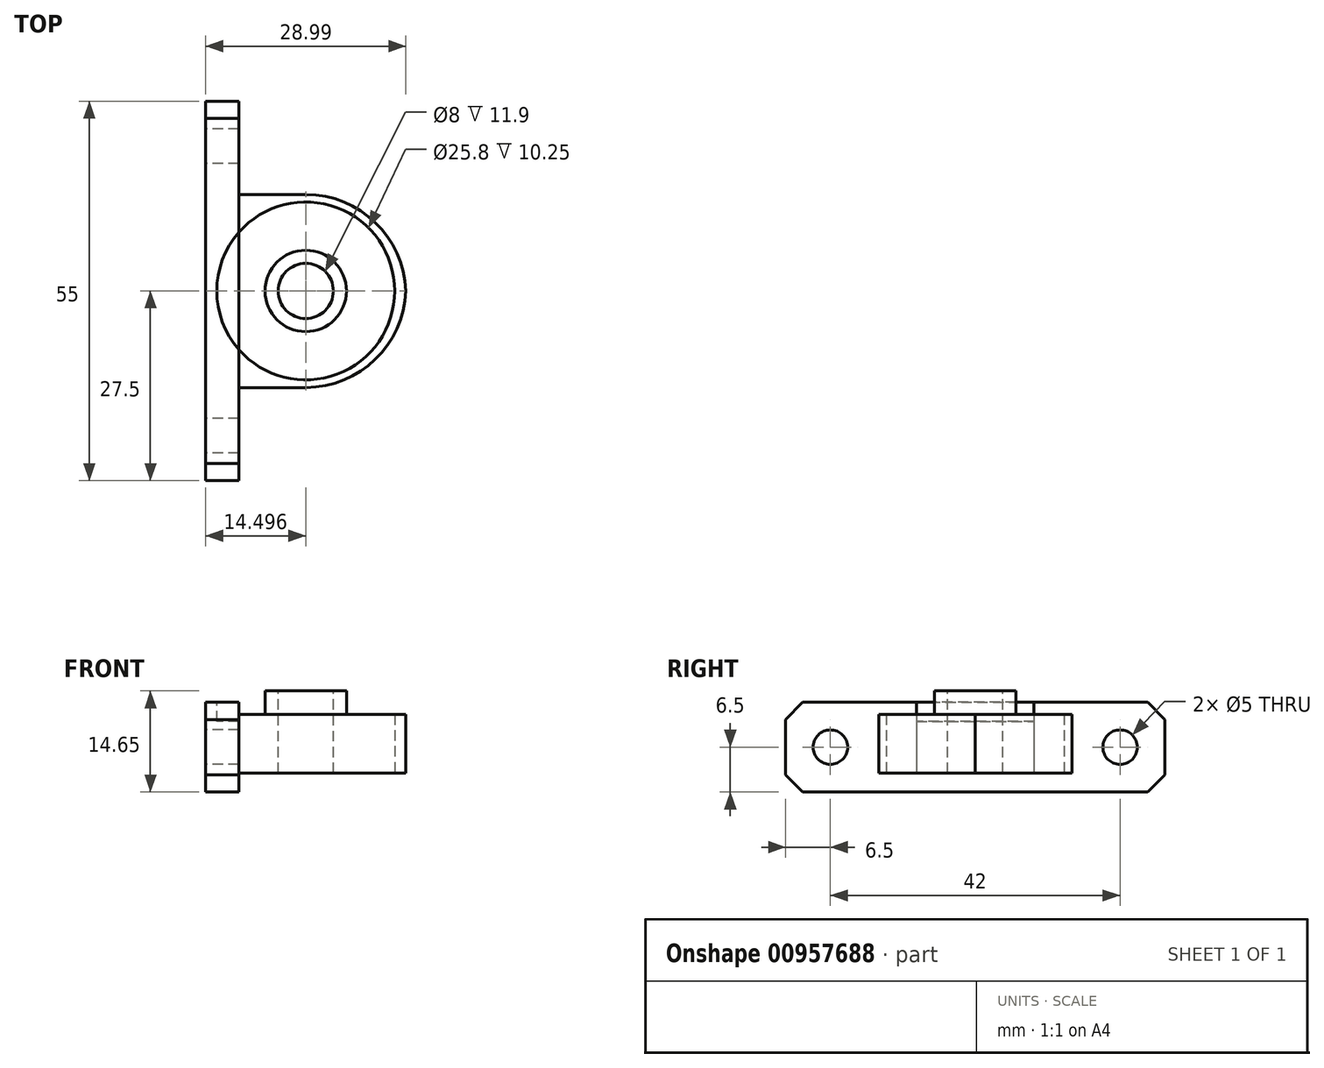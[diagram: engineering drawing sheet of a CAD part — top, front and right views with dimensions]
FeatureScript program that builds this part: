
annotation { "Feature Type Name" : "Feature", "Feature Type Description" : "" }
export const myFeature = defineFeature(function(context is Context, id is Id, definition is map)
    precondition{}
    {
        {
            var Q0;
            Q0=qCreatedBy(makeId("Right.planeOp"),FACE);
            var sketch = newSketch(context, id + "F0", { "sketchPlane" : qUnion([Q0])});
            skLineSegment(sketch, "E0.bottom", {"start": v(0, 0) * mm, "end": v(55, 0) * mm});
            skLineSegment(sketch, "E0.top", {"start": v(0, -13) * mm, "end": v(55, -13) * mm});
            skLineSegment(sketch, "E0.left", {"start": v(0, 0) * mm, "end": v(0, -13) * mm});
            skLineSegment(sketch, "E0.right", {"start": v(55, 0) * mm, "end": v(55, -13) * mm});
            skLineSegment(sketch, "E1", {"start": v(27.5, 0) * mm, "end": v(27.5, -13) * mm, "construction": true});
            skCircle(sketch, "E2", {"center": v(48.5, -6.5) * mm, "radius": 2.5 * mm});
            skLineSegment(sketch, "E3", {"start": v(0, -6.5) * mm, "end": v(55, -6.5) * mm, "construction": true});
            skCircle(sketch, "E4.MirrorC", {"center": v(6.5, -6.5) * mm, "radius": 2.5 * mm});
            skSolve(sketch);
        }
        {
            var Q0;
            Q0 = qSketchRegion(id + "F0", true);
            extrude(context, id + "F1", {"entities" : qUnion([Q0]), "depth" : 4.8 * mm, "offsetDistance" : 25 * mm});
        }
        {
            var Q0;
            Q0 = qSketchRegion(id + "F0", true);
            extrude(context, id + "F2", {"entities" : qUnion([Q0]), "operationType" : NewBodyOperationType.REMOVE, "oppositeDirection" : true, "depth" : 25 * mm, "offsetDistance" : 25 * mm});
        }
        {
            var Q0;
            Q0=makeQuery(id+"F1.opExtrude","SWEPT_EDGE",EDGE,{"disambiguationData":[OSD([sQuery(id+"F0.wireOp",EDGE,"E0.bottom"),sQuery(id+"F0.wireOp",EDGE,"E0.left")])]});
            var Q1;
            Q1=makeQuery(id+"F1.opExtrude","SWEPT_EDGE",EDGE,{"disambiguationData":[OSD([sQuery(id+"F0.wireOp",EDGE,"E0.top"),sQuery(id+"F0.wireOp",EDGE,"E0.left")])]});
            var Q2;
            Q2=makeQuery(id+"F1.opExtrude","SWEPT_EDGE",EDGE,{"disambiguationData":[OSD([sQuery(id+"F0.wireOp",EDGE,"E0.bottom"),sQuery(id+"F0.wireOp",EDGE,"E0.right")])]});
            var Q3;
            Q3=makeQuery(id+"F1.opExtrude","SWEPT_EDGE",EDGE,{"disambiguationData":[OSD([sQuery(id+"F0.wireOp",EDGE,"E0.top"),sQuery(id+"F0.wireOp",EDGE,"E0.right")])]});
            chamfer(context, id + "F3", {"entities" : qUnion([Q0, Q1, Q2, Q3]), "width" : 2.5 * mm, "tangentPropagation" : true});
        }
        {
            var Q0;
            Q0=makeQuery(id+"F1.opExtrude","CAP_FACE",FACE,{"disambiguationData":[OSD([sQuery(id+"F0.wireOp",EDGE,"E0.bottom"),sQuery(id+"F0.wireOp",EDGE,"E0.top"),sQuery(id+"F0.wireOp",EDGE,"E0.left"),sQuery(id+"F0.wireOp",EDGE,"E0.right"),sQuery(id+"F0.wireOp",EDGE,"E2"),sQuery(id+"F0.wireOp",EDGE,"E4.MirrorC")])],"isStart":false});
            var sketch = newSketch(context, id + "F4", { "sketchPlane" : qUnion([Q0])});
            skLineSegment(sketch, "E5.bottom", {"start": v(41.5, -11.25) * mm, "end": v(13.5, -11.25) * mm});
            skLineSegment(sketch, "E5.top", {"start": v(41.5, -1.75) * mm, "end": v(13.5, -1.75) * mm});
            skLineSegment(sketch, "E5.left", {"start": v(41.5, -11.25) * mm, "end": v(41.5, -1.75) * mm});
            skLineSegment(sketch, "E5.right", {"start": v(13.5, -11.25) * mm, "end": v(13.5, -1.75) * mm});
            skPoint(sketch, "E5.middle", {"position": v(27.5, -6.5) * mm});
            skPoint(sketch, "E5.middle.positionSnap0", {"position": v(0, -6.5) * mm});
            skPoint(sketch, "E5.middle.positionSnap1", {"position": v(27.5, -13) * mm});
            skPoint(sketch, "E5.centerSnap0", {"position": v(0, -6.5) * mm});
            skPoint(sketch, "E5.centerSnap1", {"position": v(27.5, -13) * mm});
            skSolve(sketch);
        }
        {
            var Q0;
            Q0 = qSketchRegion(id + "F4", true);
            extrude(context, id + "F5", {"entities" : qUnion([Q0]), "operationType" : NewBodyOperationType.ADD, "depth" : 24.2 * mm, "offsetDistance" : 25 * mm});
        }
        {
            var Q0;
            Q0=makeQuery(id+"F5.opExtrude","CAP_EDGE",EDGE,{"disambiguationData":[OSD([sQuery(id+"F4.wireOp",EDGE,"E5.right")])],"isStart":false});
            var Q1;
            Q1=makeQuery(id+"F5.opExtrude","CAP_EDGE",EDGE,{"disambiguationData":[OSD([sQuery(id+"F4.wireOp",EDGE,"E5.left")])],"isStart":false});
            fillet(context, id + "F6", {"entities" : qUnion([Q0, Q1]), "radius" : 14.5 * mm, "tangentPropagation" : true, "allowEdgeOverflow" : false});
        }
        {
            var Q0;
            Q0=makeQuery(id+"F5.opExtrude","SWEPT_FACE",FACE,{"disambiguationData":[OSD([sQuery(id+"F4.wireOp",EDGE,"E5.top")])]});
            var sketch = newSketch(context, id + "F7", { "sketchPlane" : qUnion([Q0])});
            skCircle(sketch, "E6", {"center": v(51.05, 13.98) * mm, "radius": 12.9 * mm});
            skLineSegment(sketch, "E7", {"start": v(29, 27.5) * mm, "end": v(0, 27.5) * mm, "construction": true});
            skLineSegment(sketch, "E8", {"start": v(14.5, 27.5) * mm, "end": v(14.5, 41.5) * mm, "construction": true});
            skCircle(sketch, "E9", {"center": v(14.5, 27.5) * mm, "radius": 12.9 * mm});
            skCircle(sketch, "E10", {"center": v(14.5, 27.5) * mm, "radius": 5.9 * mm});
            skSolve(sketch);
        }
        {
            var Q0;
            Q0=makeQuery(id+"F7.imprint","IMPRINT",FACE,{"disambiguationData":[TD([[makeQuery(id+"F7.imprint","IMPRINT",EDGE,{"derivedFrom":sQuery(id+"F7.wireOp",EDGE,"E10")}),-1.0]])]});
            var Q1;
            {var subQ0=sQuery(id+"F7.wireOp",EDGE,"E9");var subQ1=makeQuery(id+"F5.opExtrude","CAP_EDGE",EDGE,{"disambiguationData":[OSD([sQuery(id+"F4.wireOp",EDGE,"E5.top")])],"isStart":true});var subQ2=makeQuery(id+"F7.imprint","INTERSECT",VERTEX,{"disambiguationData":[OD(0.0)],"derivedFrom":[subQ1,subQ0]});Q1=makeQuery(id+"F7.imprint","IMPRINT",FACE,{"disambiguationData":[TD([[makeQuery(id+"F7.imprint","IMPRINT",EDGE,{"disambiguationData":[TD([[subQ2,-1.0]])],"derivedFrom":subQ0}),1.0]])]});}
            extrude(context, id + "F8", {"entities" : qUnion([Q0, Q1]), "operationType" : NewBodyOperationType.REMOVE, "oppositeDirection" : true, "depth" : 1 * mm, "offsetDistance" : 25 * mm, "hasSecondDirection" : true, "secondDirectionOppositeDirection" : false, "secondDirectionDepth" : 25 * mm});
        }
        {
            var Q0;
            Q0=makeQuery(id+"F8.boolean.opBoolean","SPLIT",FACE,{"disambiguationData":[TD([makeQuery(id+"F8.opExtrude","SWEPT_FACE",FACE,{"disambiguationData":[OSD([sQuery(id+"F7.wireOp",EDGE,"E10")])]})])],"derivedFrom":makeQuery(id+"F5.opExtrude","SWEPT_FACE",FACE,{"disambiguationData":[OSD([sQuery(id+"F4.wireOp",EDGE,"E5.top")])]})});
            var sketch = newSketch(context, id + "F9", { "sketchPlane" : qUnion([Q0])});
            skCircle(sketch, "E11", {"center": v(14.5, 27.5) * mm, "radius": 4 * mm});
            skSolve(sketch);
        }
        {
            var Q0;
            Q0 = qSketchRegion(id + "F9", true);
            extrude(context, id + "F10", {"entities" : qUnion([Q0]), "operationType" : NewBodyOperationType.REMOVE, "oppositeDirection" : true, "depth" : 25 * mm, "offsetDistance" : 25 * mm});
        }
        {
            var Q0;
            Q0=makeQuery(id+"F5.opExtrude","SWEPT_FACE",FACE,{"disambiguationData":[OSD([sQuery(id+"F4.wireOp",EDGE,"E5.bottom")])]});
            var sketch = newSketch(context, id + "F11", { "sketchPlane" : qUnion([Q0])});
            skCircle(sketch, "E12.0", {"center": v(14.5, -27.5) * mm, "radius": 12.9 * mm});
            skCircle(sketch, "E13.0", {"center": v(14.5, -27.5) * mm, "radius": 5.9 * mm});
            skSolve(sketch);
        }
        {
            var Q0;
            Q0=makeQuery(id+"F11.imprint","IMPRINT",FACE,{"disambiguationData":[TD([[makeQuery(id+"F11.imprint","IMPRINT",EDGE,{"derivedFrom":sQuery(id+"F11.wireOp",EDGE,"E13.0")}),1.0]])]});
            var Q1;
            {var subQ0=sQuery(id+"F11.wireOp",EDGE,"E12.0");var subQ1=makeQuery(id+"F5.opExtrude","CAP_EDGE",EDGE,{"disambiguationData":[OSD([sQuery(id+"F4.wireOp",EDGE,"E5.bottom")])],"isStart":true});var subQ2=makeQuery(id+"F11.imprint","INTERSECT",VERTEX,{"disambiguationData":[OD(0.0)],"derivedFrom":[subQ1,subQ0]});Q1=makeQuery(id+"F11.imprint","IMPRINT",FACE,{"disambiguationData":[TD([[makeQuery(id+"F11.imprint","IMPRINT",EDGE,{"disambiguationData":[TD([[subQ2,-1.0]])],"derivedFrom":subQ0}),-1.0]])]});}
            extrude(context, id + "F12", {"entities" : qUnion([Q0, Q1]), "operationType" : NewBodyOperationType.REMOVE, "oppositeDirection" : true, "depth" : 1 * mm, "offsetDistance" : 25 * mm, "hasSecondDirection" : true, "secondDirectionOppositeDirection" : false, "secondDirectionDepth" : 25 * mm});
        }
        {
            var Q0;
            Q0=makeQuery(id+"F12.boolean.opBoolean","SPLIT",FACE,{"disambiguationData":[TD([makeQuery(id+"F10.boolean.opBoolean","COPY",FACE,{"derivedFrom":makeQuery(id+"F10.opExtrude","SWEPT_FACE",FACE,{"disambiguationData":[OSD([sQuery(id+"F9.wireOp",EDGE,"E11")])]})})])],"derivedFrom":makeQuery(id+"F5.opExtrude","SWEPT_FACE",FACE,{"disambiguationData":[OSD([sQuery(id+"F4.wireOp",EDGE,"E5.bottom")])]})});
            var Q1;
            Q1=makeQuery(id+"F8.boolean.opBoolean","SPLIT",FACE,{"disambiguationData":[TD([makeQuery(id+"F8.opExtrude","SWEPT_FACE",FACE,{"disambiguationData":[OSD([sQuery(id+"F7.wireOp",EDGE,"E10")])]})])],"derivedFrom":makeQuery(id+"F5.opExtrude","SWEPT_FACE",FACE,{"disambiguationData":[OSD([sQuery(id+"F4.wireOp",EDGE,"E5.top")])]})});
            extrude(context, id + "F13", {"entities" : qUnion([Q0]), "endBound" : BoundingType.UP_TO_SURFACE, "oppositeDirection" : true, "depth" : 25 * mm, "endBoundEntityFace" : qUnion([Q1]), "offsetDistance" : 25 * mm});
        }
        {
            var Q0;
            Q0=makeQuery(id+"F13.opExtrude","SWEPT_BODY",BODY,{"disambiguationData":[OSD([sQuery(id+"F4.wireOp",EDGE,"E5.bottom")])]});
            var Q1;
            Q1=makeQuery(id+"F1.opExtrude","SWEPT_BODY",BODY,{"disambiguationData":[OSD([sQuery(id+"F0.wireOp",EDGE,"E0.bottom"),sQuery(id+"F0.wireOp",EDGE,"E0.top"),sQuery(id+"F0.wireOp",EDGE,"E0.left"),sQuery(id+"F0.wireOp",EDGE,"E0.right"),sQuery(id+"F0.wireOp",EDGE,"E2"),sQuery(id+"F0.wireOp",EDGE,"E4.MirrorC")])]});
            booleanBodies(context, id + "F14", {"operationType" : BooleanOperationType.SUBTRACTION, "tools" : qUnion([Q0]), "targets" : qUnion([Q1]), "keepTools" : true});
        }
        {
            var Q0;
            Q0=makeQuery(id+"F13.opExtrude","CAP_FACE",FACE,{"disambiguationData":[OSD([sQuery(id+"F4.wireOp",EDGE,"E5.bottom")])],"isStart":true});
            var Q1;
            Q1=makeQuery(id+"F12.boolean.opBoolean","COPY",FACE,{"derivedFrom":makeQuery(id+"F12.opExtrude","CAP_FACE",FACE,{"disambiguationData":[OSD([sQuery(id+"F11.wireOp",EDGE,"E12.0"),sQuery(id+"F11.wireOp",EDGE,"E13.0")])],"isStart":false})});
            extrude(context, id + "F15", {"entities" : qUnion([Q0]), "operationType" : NewBodyOperationType.REMOVE, "endBound" : BoundingType.UP_TO_SURFACE, "oppositeDirection" : true, "depth" : 25 * mm, "endBoundEntityFace" : qUnion([Q1]), "offsetDistance" : 25 * mm});
        }
        {
            var Q0;
            Q0=makeQuery(id+"F9.imprint","IMPRINT",FACE,{"disambiguationData":[TD([[makeQuery(id+"F9.imprint","IMPRINT",EDGE,{"derivedFrom":sQuery(id+"F9.wireOp",EDGE,"E11")}),-1.0]])]});
            extrude(context, id + "F16", {"entities" : qUnion([Q0]), "operationType" : NewBodyOperationType.ADD, "depth" : 3.4 * mm, "offsetDistance" : 25 * mm});
        }
    });
